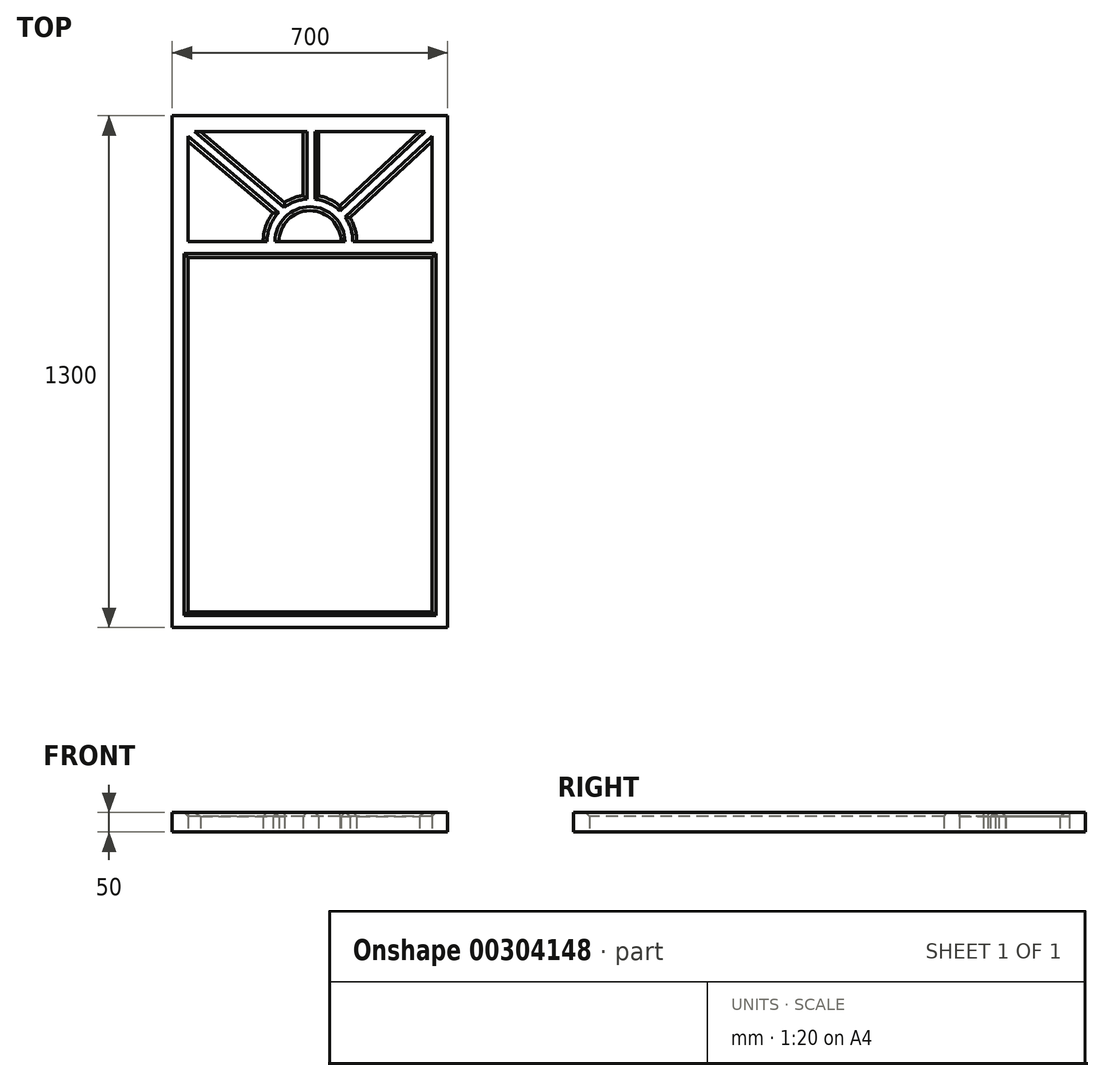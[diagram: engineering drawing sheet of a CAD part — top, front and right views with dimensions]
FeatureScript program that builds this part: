
annotation { "Feature Type Name" : "Feature", "Feature Type Description" : "" }
export const myFeature = defineFeature(function(context is Context, id is Id, definition is map)
    precondition{}
    {
        {
            var Q0;
            Q0=qCreatedBy(makeId("Top.planeOp"),FACE);
            var sketch = newSketch(context, id + "F0", { "sketchPlane" : qUnion([Q0])});
            skLineSegment(sketch, "E0.bottom", {"start": v(-362.48, 765.02) * mm, "end": v(337.52, 765.02) * mm});
            skLineSegment(sketch, "E0.top", {"start": v(-362.48, -534.98) * mm, "end": v(337.52, -534.98) * mm});
            skLineSegment(sketch, "E0.left", {"start": v(-362.48, 765.02) * mm, "end": v(-362.48, -534.98) * mm});
            skLineSegment(sketch, "E0.right", {"start": v(337.52, 765.02) * mm, "end": v(337.52, -534.98) * mm});
            skLineSegment(sketch, "E1.bottom", {"start": v(-322.48, 405.02) * mm, "end": v(297.52, 405.02) * mm});
            skLineSegment(sketch, "E1.top", {"start": v(-322.48, -494.98) * mm, "end": v(297.52, -494.98) * mm});
            skLineSegment(sketch, "E1.left", {"start": v(-322.48, 405.02) * mm, "end": v(-322.48, -494.98) * mm});
            skLineSegment(sketch, "E1.right", {"start": v(297.52, 405.02) * mm, "end": v(297.52, -494.98) * mm});
            skLineSegment(sketch, "E2", {"start": v(-322.48, 445.02) * mm, "end": v(297.52, 445.02) * mm});
            skArc(sketch, "E3", {"start": v(66.4, 445.02) * mm, "mid": v(-12.48, 523.9) * mm, "end": v(-91.35, 445.02) * mm});
            skArc(sketch, "E4", {"start": v(106.4, 445.02) * mm, "mid": v(-12.48, 563.9) * mm, "end": v(-131.35, 445.02) * mm});
            skLineSegment(sketch, "E5", {"start": v(-322.48, 445.02) * mm, "end": v(-322.48, 725.02) * mm});
            skLineSegment(sketch, "E6", {"start": v(-322.48, 725.02) * mm, "end": v(297.52, 725.02) * mm});
            skLineSegment(sketch, "E7", {"start": v(297.52, 725.02) * mm, "end": v(297.52, 445.02) * mm});
            skLineSegment(sketch, "E8", {"start": v(-77.25, 544.7) * mm, "end": v(-290.1, 725.02) * mm});
            skLineSegment(sketch, "E9", {"start": v(-290.1, 725.02) * mm, "end": v(-322.48, 725.02) * mm});
            skLineSegment(sketch, "E10", {"start": v(-322.48, 700.02) * mm, "end": v(-106.83, 517.33) * mm});
            skLineSegment(sketch, "E11", {"start": v(-30.1, 562.58) * mm, "end": v(-30.1, 725.02) * mm});
            skLineSegment(sketch, "E12", {"start": v(-30.1, 725.02) * mm, "end": v(9.9, 725.02) * mm});
            skLineSegment(sketch, "E13", {"start": v(9.9, 725.02) * mm, "end": v(9.9, 561.77) * mm});
            skLineSegment(sketch, "E14", {"start": v(63.7, 536.28) * mm, "end": v(265.69, 725.02) * mm});
            skLineSegment(sketch, "E15", {"start": v(265.69, 725.02) * mm, "end": v(297.52, 725.02) * mm});
            skLineSegment(sketch, "E16", {"start": v(297.52, 700.02) * mm, "end": v(89.67, 505.81) * mm});
            skSolve(sketch);
        }
        {
            var Q0;
            Q0=makeQuery(id+"F0.imprint","IMPRINT",FACE,{"disambiguationData":[TD([[makeQuery(id+"F0.imprint","IMPRINT",EDGE,{"derivedFrom":sQuery(id+"F0.wireOp",EDGE,"E0.bottom")}),-1.0]])]});
            var Q1;
            {var subQ1=sQuery(id+"F0.wireOp",EDGE,"E8");Q1=makeQuery(id+"F0.imprint","IMPRINT",FACE,{"disambiguationData":[TD([[makeQuery(id+"F0.imprint","IMPRINT",EDGE,{"derivedFrom":subQ1}),1.0]])]});}
            var Q2;
            {var subQ0=sQuery(id+"F0.wireOp",EDGE,"E3");Q2=makeQuery(id+"F0.imprint","IMPRINT",FACE,{"disambiguationData":[TD([[makeQuery(id+"F0.imprint","IMPRINT",EDGE,{"derivedFrom":subQ0}),-1.0]])]});}
            var Q3;
            {var subQ0=sQuery(id+"F0.wireOp",EDGE,"E11");Q3=makeQuery(id+"F0.imprint","IMPRINT",FACE,{"disambiguationData":[TD([[makeQuery(id+"F0.imprint","IMPRINT",EDGE,{"derivedFrom":subQ0}),-1.0]])]});}
            var Q4;
            {var subQ1=sQuery(id+"F0.wireOp",EDGE,"E14");Q4=makeQuery(id+"F0.imprint","IMPRINT",FACE,{"disambiguationData":[TD([[makeQuery(id+"F0.imprint","IMPRINT",EDGE,{"derivedFrom":subQ1}),-1.0]])]});}
            extrude(context, id + "F1", {"entities" : qUnion([Q0, Q1, Q2, Q3, Q4]), "depth" : 50 * mm});
        }
        {
            var Q0;
            Q0=makeQuery(id+"F1.opExtrude","CAP_EDGE",EDGE,{"disambiguationData":[OSD([sQuery(id+"F0.wireOp",EDGE,"E1.bottom")])],"isStart":false});
            var Q1;
            Q1=makeQuery(id+"F1.opExtrude","CAP_EDGE",EDGE,{"disambiguationData":[OSD([sQuery(id+"F0.wireOp",EDGE,"E1.right")])],"isStart":false});
            var Q2;
            Q2=makeQuery(id+"F1.opExtrude","CAP_EDGE",EDGE,{"disambiguationData":[OSD([sQuery(id+"F0.wireOp",EDGE,"mo2UJA6X-26PH-taNp-pn0z-x9dp37UM4p0T.bottom")])],"isStart":false});
            var Q3;
            Q3=makeQuery(id+"F1.opExtrude","CAP_EDGE",EDGE,{"disambiguationData":[OSD([sQuery(id+"F0.wireOp",EDGE,"Al6UGsGZ-SmRB-BLA8-lGx7-s1gn5zOmxmS4.right")])],"isStart":false});
            var Q4;
            Q4=makeQuery(id+"F1.opExtrude","CAP_EDGE",EDGE,{"disambiguationData":[OSD([sQuery(id+"F0.wireOp",EDGE,"Al6UGsGZ-SmRB-BLA8-lGx7-s1gn5zOmxmS4.left")])],"isStart":false});
            var Q5;
            Q5=makeQuery(id+"F1.opExtrude","CAP_EDGE",EDGE,{"disambiguationData":[OSD([sQuery(id+"F0.wireOp",EDGE,"Al6UGsGZ-SmRB-BLA8-lGx7-s1gn5zOmxmS4.top")])],"isStart":false});
            var Q6;
            Q6=makeQuery(id+"F1.opExtrude","CAP_EDGE",EDGE,{"disambiguationData":[OSD([sQuery(id+"F0.wireOp",EDGE,"Y1kuMbJq-GDfQ-tLIH-VadB-hzcVnt3jSl8J.top")])],"isStart":false});
            var Q7;
            Q7=makeQuery(id+"F1.opExtrude","CAP_EDGE",EDGE,{"disambiguationData":[OSD([sQuery(id+"F0.wireOp",EDGE,"Y1kuMbJq-GDfQ-tLIH-VadB-hzcVnt3jSl8J.right")])],"isStart":false});
            var Q8;
            Q8=makeQuery(id+"F1.opExtrude","CAP_EDGE",EDGE,{"disambiguationData":[OSD([sQuery(id+"F0.wireOp",EDGE,"Y1kuMbJq-GDfQ-tLIH-VadB-hzcVnt3jSl8J.bottom")])],"isStart":false});
            var Q9;
            Q9=makeQuery(id+"F1.opExtrude","CAP_EDGE",EDGE,{"disambiguationData":[OSD([sQuery(id+"F0.wireOp",EDGE,"Y1kuMbJq-GDfQ-tLIH-VadB-hzcVnt3jSl8J.left")])],"isStart":false});
            var Q10;
            Q10=makeQuery(id+"F1.opExtrude","CAP_EDGE",EDGE,{"disambiguationData":[OSD([sQuery(id+"F0.wireOp",EDGE,"Al6UGsGZ-SmRB-BLA8-lGx7-s1gn5zOmxmS4.bottom")])],"isStart":false});
            var Q11;
            Q11=makeQuery(id+"F1.opExtrude","CAP_EDGE",EDGE,{"disambiguationData":[OSD([sQuery(id+"F0.wireOp",EDGE,"KWYXQzDz-fkkE-oEhy-jqy3-UGAr0scdX19R.bottom")])],"isStart":false});
            var Q12;
            Q12=makeQuery(id+"F1.opExtrude","CAP_EDGE",EDGE,{"disambiguationData":[OSD([sQuery(id+"F0.wireOp",EDGE,"KWYXQzDz-fkkE-oEhy-jqy3-UGAr0scdX19R.left")])],"isStart":false});
            var Q13;
            Q13=makeQuery(id+"F1.opExtrude","CAP_EDGE",EDGE,{"disambiguationData":[OSD([sQuery(id+"F0.wireOp",EDGE,"KWYXQzDz-fkkE-oEhy-jqy3-UGAr0scdX19R.right")])],"isStart":false});
            var Q14;
            Q14=makeQuery(id+"F1.opExtrude","CAP_EDGE",EDGE,{"disambiguationData":[OSD([sQuery(id+"F0.wireOp",EDGE,"KWYXQzDz-fkkE-oEhy-jqy3-UGAr0scdX19R.top")])],"isStart":false});
            var Q15;
            Q15=makeQuery(id+"F1.opExtrude","CAP_EDGE",EDGE,{"disambiguationData":[OSD([sQuery(id+"F0.wireOp",EDGE,"mo2UJA6X-26PH-taNp-pn0z-x9dp37UM4p0T.right")])],"isStart":false});
            var Q16;
            Q16=makeQuery(id+"F1.opExtrude","CAP_EDGE",EDGE,{"disambiguationData":[OSD([sQuery(id+"F0.wireOp",EDGE,"mo2UJA6X-26PH-taNp-pn0z-x9dp37UM4p0T.top")])],"isStart":false});
            var Q17;
            Q17=makeQuery(id+"F1.opExtrude","CAP_EDGE",EDGE,{"disambiguationData":[OSD([sQuery(id+"F0.wireOp",EDGE,"mo2UJA6X-26PH-taNp-pn0z-x9dp37UM4p0T.left")])],"isStart":false});
            var Q18;
            Q18=makeQuery(id+"F1.opExtrude","CAP_EDGE",EDGE,{"disambiguationData":[OSD([sQuery(id+"F0.wireOp",EDGE,"E1.top")])],"isStart":false});
            var Q19;
            Q19=makeQuery(id+"F1.opExtrude","CAP_EDGE",EDGE,{"disambiguationData":[OSD([sQuery(id+"F0.wireOp",EDGE,"E1.left")])],"isStart":false});
            var Q20;
            Q20=makeQuery(id+"F1.opExtrude","CAP_EDGE",EDGE,{"disambiguationData":[OSD([sQuery(id+"F0.wireOp",EDGE,"E3")])],"isStart":false});
            var Q21;
            {var subQ0=sQuery(id+"F0.wireOp",EDGE,"E4");Q21=makeQuery(id+"F1.opExtrude","CAP_EDGE",EDGE,{"disambiguationData":[OSD([subQ0]),TDD([makeQuery(id+"F0.imprint","IMPRINT",EDGE,{"disambiguationData":[TD([[makeQuery(id+"F0.imprint","INTERSECT",VERTEX,{"derivedFrom":[subQ0,sQuery(id+"F0.wireOp",EDGE,"E8")]}),1.0]])],"derivedFrom":subQ0})])],"isStart":false});}
            var Q22;
            {var subQ0=sQuery(id+"F0.wireOp",EDGE,"E4");Q22=makeQuery(id+"F1.opExtrude","CAP_EDGE",EDGE,{"disambiguationData":[OSD([subQ0]),TDD([makeQuery(id+"F0.imprint","IMPRINT",EDGE,{"disambiguationData":[TD([[makeQuery(id+"F0.imprint","INTERSECT",VERTEX,{"disambiguationData":[OD(1.0)],"derivedFrom":[sQuery(id+"F0.wireOp",EDGE,"E2"),subQ0]}),1.0]])],"derivedFrom":subQ0})])],"isStart":false});}
            var Q23;
            Q23=makeQuery(id+"F1.opExtrude","CAP_EDGE",EDGE,{"disambiguationData":[OSD([sQuery(id+"F0.wireOp",EDGE,"E10")])],"isStart":false});
            var Q24;
            Q24=makeQuery(id+"F1.opExtrude","CAP_EDGE",EDGE,{"disambiguationData":[OSD([sQuery(id+"F0.wireOp",EDGE,"E8")])],"isStart":false});
            var Q25;
            Q25=makeQuery(id+"F1.opExtrude","CAP_EDGE",EDGE,{"disambiguationData":[OSD([sQuery(id+"F0.wireOp",EDGE,"E11")])],"isStart":false});
            var Q26;
            {var subQ0=sQuery(id+"F0.wireOp",EDGE,"E4");Q26=makeQuery(id+"F1.opExtrude","CAP_EDGE",EDGE,{"disambiguationData":[OSD([subQ0]),TDD([makeQuery(id+"F0.imprint","IMPRINT",EDGE,{"disambiguationData":[TD([[makeQuery(id+"F0.imprint","INTERSECT",VERTEX,{"derivedFrom":[subQ0,sQuery(id+"F0.wireOp",EDGE,"E13")]}),1.0]])],"derivedFrom":subQ0})])],"isStart":false});}
            var Q27;
            {var subQ0=sQuery(id+"F0.wireOp",EDGE,"E4");Q27=makeQuery(id+"F1.opExtrude","CAP_EDGE",EDGE,{"disambiguationData":[OSD([subQ0]),TDD([makeQuery(id+"F0.imprint","IMPRINT",EDGE,{"disambiguationData":[TD([[makeQuery(id+"F0.imprint","INTERSECT",VERTEX,{"disambiguationData":[OD(0.0)],"derivedFrom":[sQuery(id+"F0.wireOp",EDGE,"E2"),subQ0]}),-1.0]])],"derivedFrom":subQ0})])],"isStart":false});}
            var Q28;
            Q28=makeQuery(id+"F1.opExtrude","CAP_EDGE",EDGE,{"disambiguationData":[OSD([sQuery(id+"F0.wireOp",EDGE,"E16")])],"isStart":false});
            var Q29;
            Q29=makeQuery(id+"F1.opExtrude","CAP_EDGE",EDGE,{"disambiguationData":[OSD([sQuery(id+"F0.wireOp",EDGE,"E14")])],"isStart":false});
            var Q30;
            Q30=makeQuery(id+"F1.opExtrude","CAP_EDGE",EDGE,{"disambiguationData":[OSD([sQuery(id+"F0.wireOp",EDGE,"E13")])],"isStart":false});
            chamfer(context, id + "F2", {"entities" : qUnion([Q0, Q1, Q2, Q3, Q4, Q5, Q6, Q7, Q8, Q9, Q10, Q11, Q12, Q13, Q14, Q15, Q16, Q17, Q18, Q19, Q20, Q21, Q22, Q23, Q24, Q25, Q26, Q27, Q28, Q29, Q30]), "width" : 10 * mm, "tangentPropagation" : true});
        }
    });
